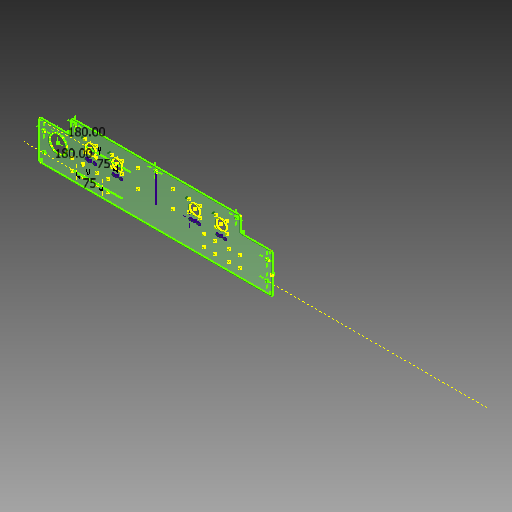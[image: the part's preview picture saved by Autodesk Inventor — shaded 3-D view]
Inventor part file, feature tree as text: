
AUTODESK INVENTOR PART (.ipt)
format: ipt  version: 2018 (Build 220112000, 112)  size: 382,976 bytes
history: native  units: in
note: dims shown in document units (in); Inventor stores cm internally (conversion verified against a paired STEP export)
features: reference x22, sketch x15, extrude x11, other x5, pattern_linear x3, hole x2, projected_geometry x1
ambient origin geometry x8: Origin, YZ Plane, XZ Plane, XY Plane, X Axis, Y Axis, Z Axis, Center Point
bodies: Solid1 (feature_tree)
feature tree (59):
  sketch  "Sketch2"  dims[d9=0.1181in d10=0.0in d11=0.1181in d12=0.0in]
  sketch  "Sketch3"  dims[d13=180.0deg d14=180.0deg]
  extrude  "Extrusion1"  Depth=0.1181in TaperAngle=0.0deg
  extrude  "Extrusion2"  TaperAngle=180.0deg  [1 undecoded]
  sketch  "Sketch5"  dims[d25=0.126in d26=0.126in]
  sketch  "Sketch6"  dims[d27=0.126in d28=0.126in]
  sketch  "Sketch7"  dims[d29=0.126in d30=0.126in]
  extrude  "Extrusion3"  Depth=2.9528in
  sketch  "Sketch9"  dims[d32=0.126in]
  hole  "Hole2"  [1 undecoded]
  hole  "Hole3"  [1 undecoded]
  sketch  "Sketch11"  dims[d42=0.1181in d43=0.2362in d44=0.1575in d45=0.0787in d46=90.0deg d47=0.315in d48=0.8108in d49=1.9685in d50=1.9685in d51=3.937in]
  extrude  "Extrusion5"  Depth=0.126in
  pattern_linear  "Rectangular Pattern1"  Count1=5  [1 undecoded]
  pattern_linear  "Rectangular Pattern2"  Count1=5  [1 undecoded]
  pattern_linear  "Rectangular Pattern3"  Count1=10  [1 undecoded]
  sketch  "Sketch14"  dims[d54=1.5748in d55=1.2224in d56=1.2224in]
  extrude  "Extrusion6"  Depth=1.2224in
  extrude  "Extrusion7"  Depth=1.2224in
  sketch  "Sketch17"  dims[d78=0.7874in d80=2.9528in d81=0.3937in d82=0.0in d83=0.3937in d84=0.0in]
  sketch  "Sketch4"  dims[d15=2.9528in d16=2.9528in]
  reference  "Reference1"
  reference  "Reference2"
  reference  "Reference3"
  reference  "Reference4"
  reference  "Reference11"
  sketch  "Sketch8"  dims[d31=0.126in]
  reference  "Reference12"
  reference  "Reference13"
  sketch  "Sketch10"  dims[d40=0.3937in d41=0.0in]
  projected_geometry  "Projected Loop1"
  sketch  "Sketch13"  dims[d52=1.2224in d53=1.2224in]
  sketch  "Sketch15"  dims[d57=0.1181in d58=0.2362in d59=0.1575in d60=0.0787in d61=90.0deg d62=0.315in d63=0.8108in d70=0.3937in d71=0.0in]
  reference  "Reference14"
  reference  "Reference15"
  reference  "Reference16"
  reference  "Reference17"
  reference  "Reference18"
  reference  "Reference19"
  reference  "Reference20"
  reference  "Reference21"
  reference  "Reference22"
  reference  "Reference23"
  reference  "Reference24"
  reference  "Reference25"
  reference  "Reference26"
  reference  "Reference27"
  sketch  "Sketch16"  dims[d72=0.7874in d74=2.9528in d75=0.7874in d77=11.5748in]
  reference  "Reference28"
  other  "<userpath>\OneDrive\Inventor\Beast 3D Printer\Extruder Assembly.iam"
  extrude  "Extruder Assembly.iam"  Depth=0.3937in TaperAngle=0.0deg
  extrude  "Extruder and Arm Sub Ass_CPY1:1"  Depth=11.5748in
  other  "Spring Block_CPY1:1"
  extrude  "Extruder Arm_CPY1:1"  Depth=0.3937in TaperAngle=0.0deg
  extrude  "Extruder and Arm Sub Ass_CPY2:1"  Depth=0.3937in TaperAngle=0.0deg
  other  "Spring Block_CPY2:1"
  extrude  "Extruder Arm_CPY2:1"  [1 undecoded]
  other  "Stepper Motor - Nema 17_CPY1:1"
  other  "Stepper Motor - Nema 17_CPY2:1"
note: 7 required parameter values undecoded (feature->parameter linkage not recoverable at this tier; creation-order binding heuristic only, values carry confidence <= 0.55)
